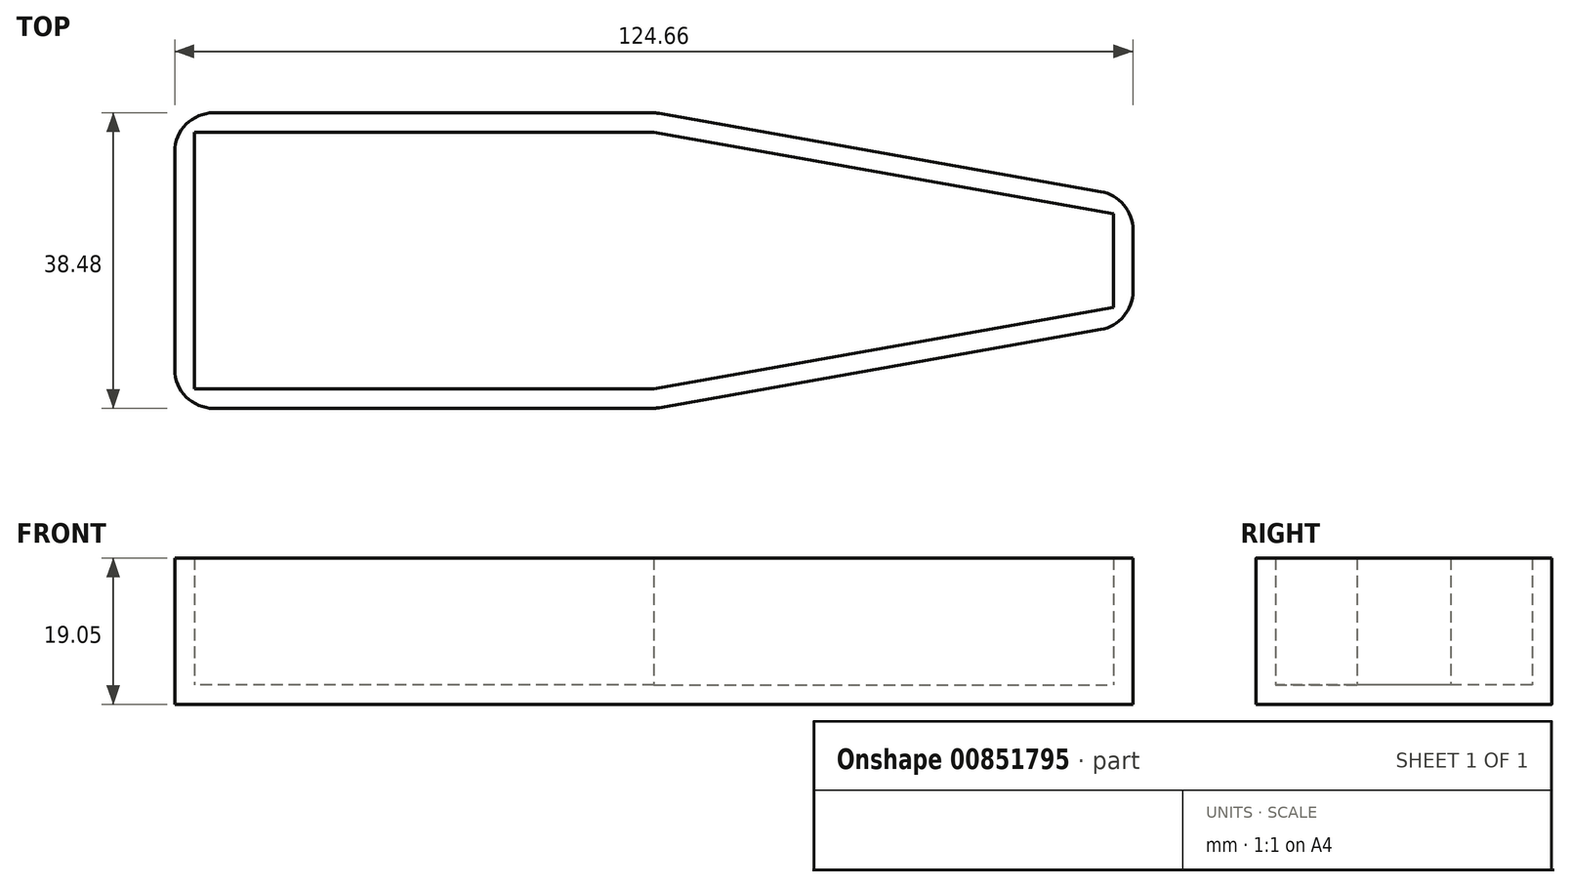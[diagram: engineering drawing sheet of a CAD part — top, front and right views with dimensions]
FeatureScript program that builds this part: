
annotation { "Feature Type Name" : "Feature", "Feature Type Description" : "" }
export const myFeature = defineFeature(function(context is Context, id is Id, definition is map)
    precondition{}
    {
        {
            var Q0;
            Q0=qCreatedBy(makeId("Top.planeOp"),FACE);
            var sketch = newSketch(context, id + "F0", { "sketchPlane" : qUnion([Q0])});
            skLineSegment(sketch, "E0.left", {"start": v(-59.8, 16.7) * mm, "end": v(-59.8, -16.7) * mm});
            skPoint(sketch, "E0.middle", {"position": v(0, 0) * mm});
            skPoint(sketch, "E1", {"position": v(0, 16.7) * mm});
            skPoint(sketch, "E2.MirrorP", {"position": v(0, -16.7) * mm});
            skPoint(sketch, "E3", {"position": v(59.8, 0) * mm});
            skPoint(sketch, "E4", {"position": v(59.8, 6.1) * mm});
            skPoint(sketch, "E5.MirrorP", {"position": v(59.8, -6.1) * mm});
            skLineSegment(sketch, "E6", {"start": v(0, -16.7) * mm, "end": v(59.8, -6.1) * mm});
            skLineSegment(sketch, "E7", {"start": v(0, 16.7) * mm, "end": v(-59.8, 16.7) * mm});
            skLineSegment(sketch, "E8", {"start": v(0, -16.7) * mm, "end": v(-59.8, -16.7) * mm});
            skLineSegment(sketch, "E9", {"start": v(59.8, 6.1) * mm, "end": v(59.8, -6.1) * mm});
            skLineSegment(sketch, "E10.bottom", {"start": v(-59.8, 16.7) * mm, "end": v(0, 16.7) * mm});
            skLineSegment(sketch, "E10.top", {"start": v(-59.8, -16.7) * mm, "end": v(0, -16.7) * mm});
            skLineSegment(sketch, "E11", {"start": v(0, 16.7) * mm, "end": v(59.8, 6.1) * mm});
            skSolve(sketch);
        }
        {
            var Q0;
            Q0 = qSketchRegion(id + "F0", true);
            extrude(context, id + "F1", {"entities" : qUnion([Q0]), "endBound" : BoundingType.SYMMETRIC, "depth" : 16.5 * mm, "offsetDistance" : 25.4 * mm});
        }
        {
            var Q0;
            Q0=makeQuery(id+"F1.opExtrude","CAP_FACE",FACE,{"disambiguationData":[OSD([sQuery(id+"F0.wireOp",EDGE,"E6"),sQuery(id+"F0.wireOp",EDGE,"E9"),sQuery(id+"F0.wireOp",EDGE,"E10.bottom"),sQuery(id+"F0.wireOp",EDGE,"E10.top"),sQuery(id+"F0.wireOp",EDGE,"E0.left"),sQuery(id+"F0.wireOp",EDGE,"E11")])],"isStart":false});
            shell(context, id + "F2", {"entities" : qUnion([Q0]), "thickness" : 2.54 * mm, "oppositeDirection" : true});
        }
        {
            var Q0;
            Q0=makeQuery(id+"F1.opExtrude","SWEPT_EDGE",EDGE,{"disambiguationData":[OSD([sQuery(id+"F0.wireOp",EDGE,"E6"),sQuery(id+"F0.wireOp",EDGE,"E9")])]});
            var Q1;
            Q1=makeQuery(id+"F1.opExtrude","SWEPT_EDGE",EDGE,{"disambiguationData":[OSD([sQuery(id+"F0.wireOp",EDGE,"E9"),sQuery(id+"F0.wireOp",EDGE,"E11")])]});
            var Q2;
            Q2=makeQuery(id+"F1.opExtrude","SWEPT_EDGE",EDGE,{"disambiguationData":[OSD([sQuery(id+"F0.wireOp",EDGE,"E10.top"),sQuery(id+"F0.wireOp",EDGE,"E0.left")])]});
            var Q3;
            Q3=makeQuery(id+"F1.opExtrude","SWEPT_EDGE",EDGE,{"disambiguationData":[OSD([sQuery(id+"F0.wireOp",EDGE,"E10.bottom"),sQuery(id+"F0.wireOp",EDGE,"E0.left")])]});
            var Q4;
            Q4=makeQuery(id+"F1.opExtrude","SWEPT_EDGE",EDGE,{"disambiguationData":[OSD([sQuery(id+"F0.wireOp",EDGE,"E6"),sQuery(id+"F0.wireOp",EDGE,"E10.top")])]});
            var Q5;
            Q5=makeQuery(id+"F1.opExtrude","SWEPT_EDGE",EDGE,{"disambiguationData":[OSD([sQuery(id+"F0.wireOp",EDGE,"E10.bottom"),sQuery(id+"F0.wireOp",EDGE,"E11")])]});
            fillet(context, id + "F3", {"entities" : qUnion([Q0, Q1, Q2, Q3, Q4, Q5]), "radius" : 5.08 * mm, "tangentPropagation" : true, "allowEdgeOverflow" : false});
        }
    });
